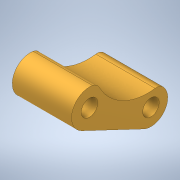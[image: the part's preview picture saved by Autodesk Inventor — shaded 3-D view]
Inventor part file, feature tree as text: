
AUTODESK INVENTOR PART (.ipt)
format: ipt  version: 2020 (Build 240168000, 168)  size: 165,888 bytes
history: native  units: in
note: dims shown in document units (in); Inventor stores cm internally (conversion verified against a paired STEP export)
features: extrude x4, sketch x4, projected_geometry x2, fillet x1
ambient origin geometry x8: Origin, YZ Plane, XZ Plane, XY Plane, X Axis, Y Axis, Z Axis, Center Point
bodies: Solid1 (feature_tree)
feature tree (11):
  extrude  "Extrusion1"  Depth=0.4523in
  extrude  "Extrusion2"  Depth=0.2118in
  extrude  "Extrusion3"  Depth=0.748in TaperAngle=0.0deg
  extrude  "Extrusion4"  Depth=0.1181in
  fillet  "Fillet1"  Radius=0.1575in
  sketch  "Sketch1"  dims[d0=0.2087in d1=0.2087in d3=0.4523in]
  sketch  "Sketch2"  dims[d4=0.2118in d5=0.8586in]
  projected_geometry  "Projected Loop1"
  sketch  "Sketch3"  dims[d6=0.8656in d7=0.748in d8=0.0in]
  sketch  "Sketch4"  dims[d11=0.0787in d12=0.315in d13=0.1575in d14=0.0in d15=0.1969in d16=0.0787in d17=0.0in d20=0.7087in d21=0.4228in d22=0.689in d23=0.0in d24=0.0in d25=0.1181in]
  projected_geometry  "Projected Loop2"
